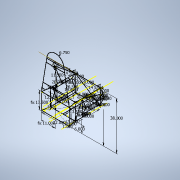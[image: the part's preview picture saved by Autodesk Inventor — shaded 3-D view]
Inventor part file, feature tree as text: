
AUTODESK INVENTOR PART (.ipt)
format: ipt  version: 2021 (Build 250183000, 183)  size: 210,432 bytes
history: native  units: in
note: dims shown in document units (in); Inventor stores cm internally (conversion verified against a paired STEP export)
features: sketch x17, plane x17, other x1
ambient origin geometry x8: Origin, YZ Plane, XZ Plane, XY Plane, X Axis, Y Axis, Z Axis, Center Point
feature tree (35):
  sketch  "Sketch1"  dims[d0=22.0in d1=6.75in d2=26.5in d3=20.0in d4=35.0in d5=38.0in d6=13.5in d7=13.5in d8=13.0in d9=22.0in]
  plane  "Work Plane2"
  sketch  "Sketch5"  dims[d11=10.0in]
  plane  "Work Plane1"
  sketch  "Sketch3"  dims[d10=11.0in]
  plane  "Work Plane3"
  sketch  "Sketch6"  dims[d12=20.0in]
  plane  "Work Plane4"
  sketch  "Sketch7"  dims[d16=14.625in]
  plane  "Work Plane5"
  sketch  "Sketch8"  dims[d17=2.0in]
  plane  "Work Plane7"
  sketch  "Sketch9"  dims[d18=-6.5in]
  plane  "Work Plane8"
  sketch  "Sketch10"  dims[d19=6.0in]
  plane  "Work Plane9"
  sketch  "Sketch11"  dims[d20=1.0in]
  plane  "Work Plane10"
  sketch  "Sketch13"  dims[d21=20.0in]
  plane  "Work Plane11"
  sketch  "Sketch14"  dims[d22=13.0in d25=-26.0in]
  plane  "Work Plane12"
  sketch  "Sketch15"  dims[d26=20.0in]
  plane  "Work Plane13"
  sketch  "Sketch16"  dims[d29=13.5in]
  plane  "Work Plane15"
  sketch  "Sketch17"  dims[d30=20.0in]
  plane  "Work Plane16"
  sketch  "Sketch18"  dims[d31=13.0in]
  plane  "Work Plane17"
  sketch  "Sketch19"  dims[d32=14.625in]
  plane  "Work Plane18"
  sketch  "Sketch20"  dims[d33=0.5in d34=13.5in d35=13.5in d36=-10.0in d37=20.0in d38=14.625in d39=2.0in d40=20.0in d41=13.5in d42=13.0in d43=14.625in d44=0.5in d47=8.0in d48=3.0in d49=3.0in d50=2.0in d51=2.0in d52=1.25in d53=1.25in d54=15.625in d55=0.5in d56=2.0in d58=2.0in d59=1.25in d60=2.0in d61=1.25in d62=0.8532in d63=11.5in d65=0.5in d66=-0.8532in d67=11.5in d68=7.3125in d69=0.5in d70=20.5in d74=20.0in d75=3.0in d76=3.0in d77=3.0in d78=5.0in d79=8.0in d80=1.5in d81=7.8125in d82=20.5in d83=0.75in d84=0.75in]
  other  "Work Axis1"
  plane  "Work Plane14"
